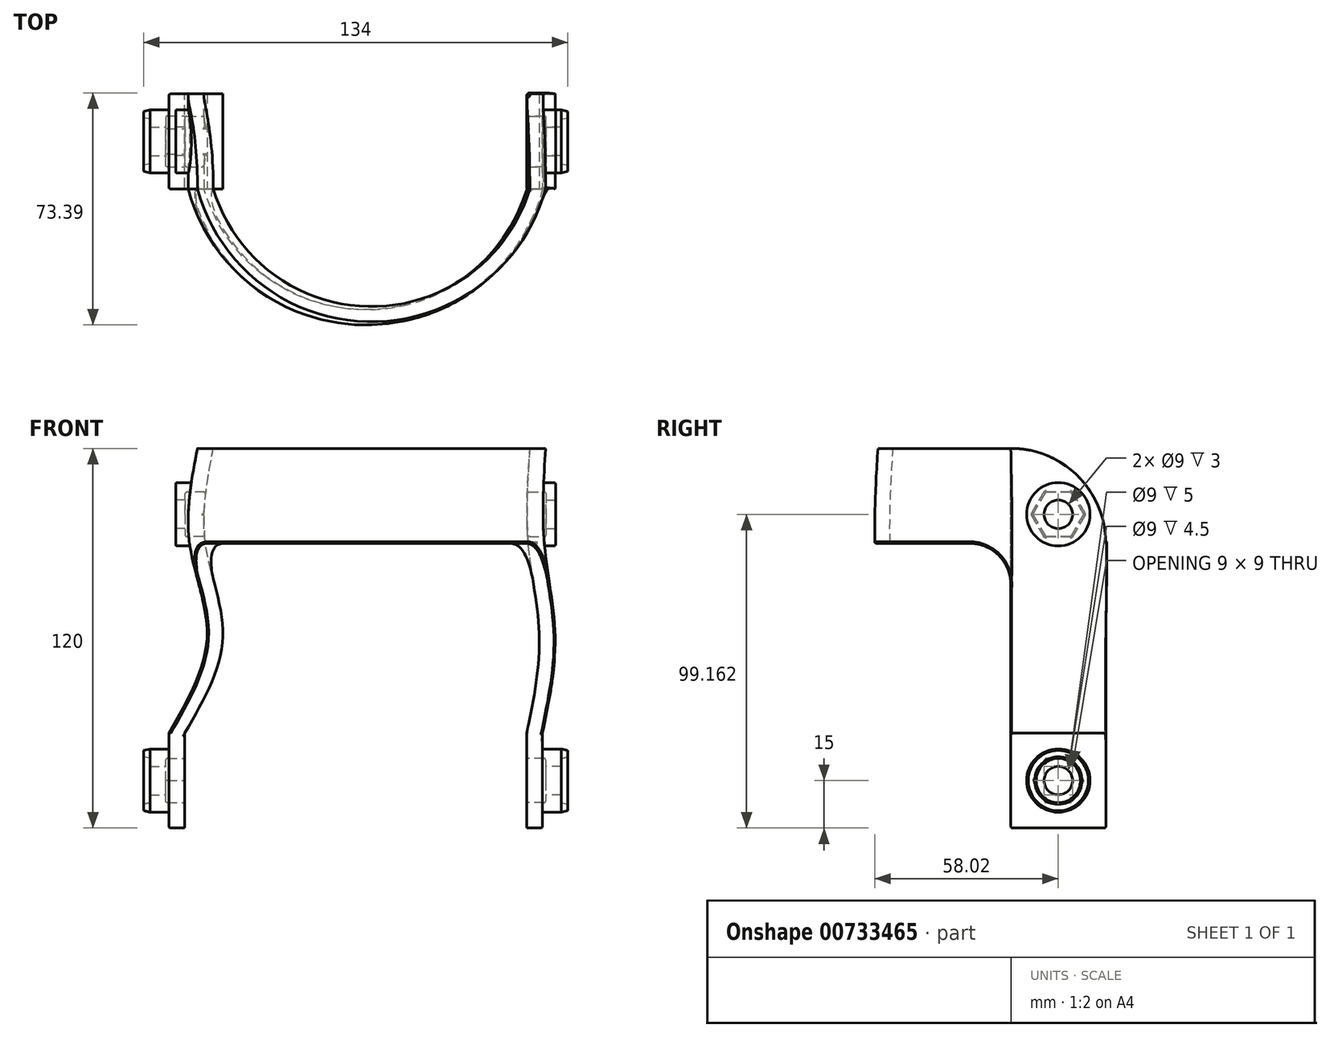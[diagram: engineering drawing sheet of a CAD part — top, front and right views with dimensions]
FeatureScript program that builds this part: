
annotation { "Feature Type Name" : "Feature", "Feature Type Description" : "" }
export const myFeature = defineFeature(function(context is Context, id is Id, definition is map)
    precondition{}
    {
        {
            var Q0;
            Q0=qCreatedBy(makeId("Top.planeOp"),FACE);
            cPlane(context, id + "F0", {"entities" : qUnion([Q0]), "cplaneType" : CPlaneType.OFFSET, "offset" : 30 * mm, "width" : 150 * mm, "height" : 150 * mm});
        }
        {
            var Q0;
            Q0=qCreatedBy(id+"F0.planeOp",FACE);
            var sketch = newSketch(context, id + "F1", { "sketchPlane" : qUnion([Q0])});
            skLineSegment(sketch, "E0", {"start": v(-54, 0) * mm, "end": v(-54, 15) * mm});
            skLineSegment(sketch, "E1", {"start": v(-54, 15) * mm, "end": v(-59, 15) * mm});
            skLineSegment(sketch, "E2", {"start": v(-59, 15) * mm, "end": v(-59, -15) * mm});
            skLineSegment(sketch, "E3", {"start": v(-54, -15) * mm, "end": v(-54, 0) * mm});
            skLineSegment(sketch, "E4", {"start": v(54, 0) * mm, "end": v(54, 15) * mm});
            skLineSegment(sketch, "E5", {"start": v(54, 15) * mm, "end": v(59, 15) * mm});
            skLineSegment(sketch, "E6", {"start": v(59, 15) * mm, "end": v(59, -15) * mm});
            skLineSegment(sketch, "E7", {"start": v(54, -15) * mm, "end": v(54, 0) * mm});
            skArc(sketch, "E8", {"start": v(-54, -15) * mm, "mid": v(0, -56.04) * mm, "end": v(54, -15) * mm});
            skArc(sketch, "E9", {"start": v(59, -15) * mm, "mid": v(0, -60.88) * mm, "end": v(-59, -15) * mm});
            skPoint(sketch, "E10", {"position": v(0, -56.04) * mm});
            skPoint(sketch, "E11", {"position": v(0, -60.88) * mm});
            skSolve(sketch);
        }
        {
            var Q0;
            Q0=qCreatedBy(makeId("Top.planeOp"),FACE);
            var sketch = newSketch(context, id + "F2", { "sketchPlane" : qUnion([Q0])});
            skLineSegment(sketch, "E12", {"start": v(-54, 0) * mm, "end": v(-54, 15) * mm});
            skLineSegment(sketch, "E13", {"start": v(-54, 15) * mm, "end": v(-59, 15) * mm});
            skLineSegment(sketch, "E14", {"start": v(-59, 15) * mm, "end": v(-59, -15) * mm});
            skLineSegment(sketch, "E15", {"start": v(-54, -15) * mm, "end": v(-54, 0) * mm});
            skLineSegment(sketch, "E16", {"start": v(54, 0) * mm, "end": v(54, 15) * mm});
            skLineSegment(sketch, "E17", {"start": v(54, 15) * mm, "end": v(59, 15) * mm});
            skLineSegment(sketch, "E18", {"start": v(59, 15) * mm, "end": v(59, -15) * mm});
            skLineSegment(sketch, "E19", {"start": v(54, -15) * mm, "end": v(54, 0) * mm});
            skArc(sketch, "E20", {"start": v(-54, -15) * mm, "mid": v(0, -56.04) * mm, "end": v(54, -15) * mm});
            skArc(sketch, "E21", {"start": v(59, -15) * mm, "mid": v(0, -60.88) * mm, "end": v(-59, -15) * mm});
            skPoint(sketch, "E22", {"position": v(0, -56.04) * mm});
            skPoint(sketch, "E23", {"position": v(0, -60.88) * mm});
            skSolve(sketch);
        }
        {
            var Q0;
            Q0=qCreatedBy(makeId("Top.planeOp"),FACE);
            cPlane(context, id + "F3", {"entities" : qUnion([Q0]), "cplaneType" : CPlaneType.OFFSET, "offset" : 60 * mm, "width" : 150 * mm, "height" : 150 * mm});
        }
        {
            var Q0;
            Q0=qCreatedBy(id+"F3.planeOp",FACE);
            var sketch = newSketch(context, id + "F4", { "sketchPlane" : qUnion([Q0])});
            skPoint(sketch, "E24", {"position": v(8, 0) * mm});
            skPoint(sketch, "E25", {"position": v(-42, 0) * mm});
            skPoint(sketch, "E26", {"position": v(58, 0) * mm});
            skLineSegment(sketch, "E27", {"start": v(-42, 0) * mm, "end": v(-42, -15) * mm});
            skLineSegment(sketch, "E28", {"start": v(-47, -15) * mm, "end": v(-47, 15) * mm});
            skLineSegment(sketch, "E29", {"start": v(-47, 15) * mm, "end": v(-42, 15) * mm});
            skLineSegment(sketch, "E30", {"start": v(-42, 15) * mm, "end": v(-42, 0) * mm});
            skLineSegment(sketch, "E31", {"start": v(58, 0) * mm, "end": v(58, 15) * mm});
            skLineSegment(sketch, "E32", {"start": v(58, 15) * mm, "end": v(63, 15) * mm});
            skLineSegment(sketch, "E33", {"start": v(63, 15) * mm, "end": v(63, -15) * mm});
            skLineSegment(sketch, "E34", {"start": v(58, -15) * mm, "end": v(58, 0) * mm});
            skArc(sketch, "E35", {"start": v(-42, -15) * mm, "mid": v(8, -52.2) * mm, "end": v(58, -15) * mm});
            skArc(sketch, "E36", {"start": v(-47, -15) * mm, "mid": v(8, -57) * mm, "end": v(63, -15) * mm});
            skSolve(sketch);
        }
        {
            var Q0;
            Q0=qCreatedBy(makeId("Top.planeOp"),FACE);
            cPlane(context, id + "F5", {"entities" : qUnion([Q0]), "cplaneType" : CPlaneType.OFFSET, "offset" : 90 * mm, "width" : 150 * mm, "height" : 150 * mm});
        }
        {
            var Q0;
            Q0=qCreatedBy(id+"F5.planeOp",FACE);
            var sketch = newSketch(context, id + "F6", { "sketchPlane" : qUnion([Q0])});
            skPoint(sketch, "E37", {"position": v(3.5, 0) * mm});
            skPoint(sketch, "E38", {"position": v(-47.5, 0) * mm});
            skPoint(sketch, "E39", {"position": v(54.5, 0) * mm});
            skLineSegment(sketch, "E40", {"start": v(-47.5, 0) * mm, "end": v(-47.5, 15) * mm});
            skLineSegment(sketch, "E41", {"start": v(-47.5, 15) * mm, "end": v(-52.5, 15) * mm});
            skLineSegment(sketch, "E42", {"start": v(-52.5, 15) * mm, "end": v(-52.5, -15) * mm});
            skLineSegment(sketch, "E43", {"start": v(-47.5, -15) * mm, "end": v(-47.5, 0) * mm});
            skLineSegment(sketch, "E44", {"start": v(54.5, 0) * mm, "end": v(54.5, 15.37) * mm});
            skLineSegment(sketch, "E45", {"start": v(54.5, 15.37) * mm, "end": v(59.6, 15.37) * mm});
            skLineSegment(sketch, "E46", {"start": v(59.6, 15.37) * mm, "end": v(59.6, -14.63) * mm});
            skLineSegment(sketch, "E47", {"start": v(54.5, -15) * mm, "end": v(54.5, 0) * mm});
            skArc(sketch, "E48", {"start": v(-47.5, -15) * mm, "mid": v(3.5, -53.16) * mm, "end": v(54.5, -15) * mm});
            skArc(sketch, "E49", {"start": v(-52.5, -15) * mm, "mid": v(3.69, -57.97) * mm, "end": v(59.6, -14.63) * mm});
            skSolve(sketch);
        }
        {
            var Q0;
            Q0=qCreatedBy(makeId("Top.planeOp"),FACE);
            cPlane(context, id + "F7", {"entities" : qUnion([Q0]), "cplaneType" : CPlaneType.OFFSET, "offset" : 120 * mm, "width" : 150 * mm, "height" : 150 * mm});
        }
        {
            var Q0;
            Q0=qCreatedBy(id+"F7.planeOp",FACE);
            var sketch = newSketch(context, id + "F8", { "sketchPlane" : qUnion([Q0])});
            skPoint(sketch, "E50", {"position": v(5, 0) * mm});
            skPoint(sketch, "E51", {"position": v(-45, 0) * mm});
            skPoint(sketch, "E52", {"position": v(55, 0) * mm});
            skLineSegment(sketch, "E53", {"start": v(-45, 0) * mm, "end": v(-45, 15) * mm});
            skLineSegment(sketch, "E54", {"start": v(-45, 15) * mm, "end": v(-50, 15) * mm});
            skLineSegment(sketch, "E55", {"start": v(-50, 15) * mm, "end": v(-50, -15) * mm});
            skLineSegment(sketch, "E56", {"start": v(-45, -15) * mm, "end": v(-45, 0) * mm});
            skLineSegment(sketch, "E57", {"start": v(55, 0) * mm, "end": v(55, -15) * mm});
            skLineSegment(sketch, "E58", {"start": v(60, -15) * mm, "end": v(60, 15) * mm});
            skLineSegment(sketch, "E59", {"start": v(60, 15) * mm, "end": v(55, 15) * mm});
            skLineSegment(sketch, "E60", {"start": v(55, 15) * mm, "end": v(55, 0) * mm});
            skArc(sketch, "E61", {"start": v(-45, -15) * mm, "mid": v(5, -52.2) * mm, "end": v(55, -15) * mm});
            skArc(sketch, "E62", {"start": v(-50, -15) * mm, "mid": v(5, -57) * mm, "end": v(60, -15) * mm});
            skSolve(sketch);
        }
        {
            var Q0;
            Q0=makeQuery(id+"F1.imprint","IMPRINT",FACE,{"disambiguationData":[TD([[makeQuery(id+"F1.imprint","IMPRINT",EDGE,{"derivedFrom":sQuery(id+"F1.wireOp",EDGE,"E0")}),1.0]])]});
            var Q1;
            Q1=makeQuery(id+"F4.imprint","IMPRINT",FACE,{"disambiguationData":[TD([[makeQuery(id+"F4.imprint","IMPRINT",EDGE,{"derivedFrom":sQuery(id+"F4.wireOp",EDGE,"E27")}),-1.0]])]});
            var Q2;
            Q2=makeQuery(id+"F6.imprint","IMPRINT",FACE,{"disambiguationData":[TD([[makeQuery(id+"F6.imprint","IMPRINT",EDGE,{"derivedFrom":sQuery(id+"F6.wireOp",EDGE,"E40")}),1.0]])]});
            var Q3;
            Q3=makeQuery(id+"F8.imprint","IMPRINT",FACE,{"disambiguationData":[TD([[makeQuery(id+"F8.imprint","IMPRINT",EDGE,{"derivedFrom":sQuery(id+"F8.wireOp",EDGE,"E53")}),1.0]])]});
            loft(context, id + "F9", {"sheetProfilesArray" : [{ "sheetProfileEntities" : qUnion([Q0]) }, { "sheetProfileEntities" : qUnion([Q1]) }, { "sheetProfileEntities" : qUnion([Q2]) }, { "sheetProfileEntities" : qUnion([Q3]) }]});
        }
        {
            var Q0;
            Q0=makeQuery(id+"F2.imprint","IMPRINT",FACE,{"disambiguationData":[TD([[makeQuery(id+"F2.imprint","IMPRINT",EDGE,{"derivedFrom":sQuery(id+"F2.wireOp",EDGE,"E12")}),1.0]])]});
            extrude(context, id + "F10", {"entities" : qUnion([Q0]), "operationType" : NewBodyOperationType.ADD, "depth" : 30 * mm, "offsetDistance" : 25 * mm});
        }
        {
            var Q0;
            Q0=qCreatedBy(makeId("Right.planeOp"),FACE);
            var sketch = newSketch(context, id + "F11", { "sketchPlane" : qUnion([Q0])});
            skPoint(sketch, "E63", {"position": v(82.65, 59.89) * mm});
            skPoint(sketch, "E64", {"position": v(-15, 120) * mm});
            skPoint(sketch, "E65", {"position": v(-15, 90) * mm});
            skArc(sketch, "E66", {"start": v(-15, 120) * mm, "mid": v(6.21, 111.21) * mm, "end": v(15, 90) * mm});
            skPoint(sketch, "E67", {"position": v(-28.01, 76.99) * mm});
            skArc(sketch, "E68", {"start": v(-15, 76.99) * mm, "mid": v(-18.81, 86.19) * mm, "end": v(-28.01, 90) * mm});
            skLineSegment(sketch, "E69", {"start": v(-15, 76.99) * mm, "end": v(-15, -61.51) * mm});
            skLineSegment(sketch, "E70", {"start": v(-15, -61.51) * mm, "end": v(-141.22, -61.51) * mm});
            skLineSegment(sketch, "E71", {"start": v(-141.22, -61.51) * mm, "end": v(-141.22, 174.74) * mm});
            skLineSegment(sketch, "E72", {"start": v(-141.22, 174.74) * mm, "end": v(85.32, 174.74) * mm});
            skLineSegment(sketch, "E73", {"start": v(85.32, 174.74) * mm, "end": v(15, 90) * mm});
            skLineSegment(sketch, "E74", {"start": v(-28.01, 90) * mm, "end": v(-81.35, 90) * mm});
            skLineSegment(sketch, "E75", {"start": v(-81.35, 90) * mm, "end": v(-81.35, 120) * mm});
            skLineSegment(sketch, "E76", {"start": v(-81.35, 120) * mm, "end": v(-15, 120) * mm});
            skSolve(sketch);
        }
        {
            var Q0;
            Q0=qSketchRegion(id+"F11",true);
            extrude(context, id + "F12", {"entities" : qUnion([Q0]), "operationType" : NewBodyOperationType.REMOVE, "oppositeDirection" : true, "depth" : 100 * mm, "offsetDistance" : 25 * mm, "hasSecondDirection" : true, "secondDirectionOppositeDirection" : false, "secondDirectionDepth" : 100 * mm});
        }
        {
            var Q0;
            Q0=makeQuery(id+"F10.opExtrude","SWEPT_FACE",FACE,{"disambiguationData":[OSD([sQuery(id+"F2.wireOp",EDGE,"E14")])]});
            var sketch = newSketch(context, id + "F13", { "sketchPlane" : qUnion([Q0])});
            skPoint(sketch, "E77", {"position": v(0, 15) * mm});
            skCircle(sketch, "E78", {"center": v(0, 15) * mm, "radius": 10 * mm});
            skSolve(sketch);
        }
        {
            var Q0;
            Q0=makeQuery(id+"F13.imprint","IMPRINT",FACE,{"disambiguationData":[TD([[makeQuery(id+"F13.imprint","IMPRINT",EDGE,{"derivedFrom":sQuery(id+"F13.wireOp",EDGE,"E78")}),1.0]])]});
            extrude(context, id + "F14", {"entities" : qUnion([Q0]), "operationType" : NewBodyOperationType.ADD, "depth" : 6 * mm, "offsetDistance" : 25 * mm});
        }
        {
            var Q0;
            Q0=qCreatedBy(makeId("Front.planeOp"),FACE);
            var sketch = newSketch(context, id + "F15", { "sketchPlane" : qUnion([Q0])});
            skPoint(sketch, "E79", {"position": v(-54, 15) * mm});
            skPoint(sketch, "E80", {"position": v(-49.01, 23.39) * mm});
            skPoint(sketch, "E81", {"position": v(-65, 15) * mm});
            skLineSegment(sketch, "E82", {"start": v(-65, 22) * mm, "end": v(-65, 25) * mm});
            skLineSegment(sketch, "E83", {"start": v(-65, 25) * mm, "end": v(-67, 24.5) * mm});
            skLineSegment(sketch, "E84", {"start": v(-67, 24.5) * mm, "end": v(-67, 22.5) * mm});
            skLineSegment(sketch, "E85", {"start": v(-67, 22.5) * mm, "end": v(-65, 22) * mm});
            skPoint(sketch, "E86", {"position": v(-65, 23.5) * mm});
            skPoint(sketch, "E87", {"position": v(-67, 23.5) * mm});
            skLineSegment(sketch, "E88", {"start": v(-65, 15) * mm, "end": v(-67, 15) * mm});
            skLineSegment(sketch, "E89", {"start": v(-65, 22) * mm, "end": v(-67, 22.5) * mm});
            skLineSegment(sketch, "E90", {"start": v(-67, 22.5) * mm, "end": v(-67, 24.5) * mm});
            skLineSegment(sketch, "E91", {"start": v(-67, 24.5) * mm, "end": v(-65, 25) * mm});
            skLineSegment(sketch, "E92", {"start": v(-65, 25) * mm, "end": v(-65, 22) * mm});
            skSolve(sketch);
        }
        {
            var Q0;
            Q0=qSketchRegion(id+"F15",true);
            var Q1;
            Q1=sQuery(id+"F15.wireOp",EDGE,"E88");
            revolve(context, id + "F16", {"operationType" : NewBodyOperationType.ADD, "surfaceOperationType" : NewSurfaceOperationType.NEW, "entities" : qUnion([Q0]), "axis" : qUnion([Q1]), "revolveType" : RevolveType.FULL});
        }
        {
            var Q0;
            Q0=makeQuery(id+"F10.opExtrude","SWEPT_FACE",FACE,{"disambiguationData":[OSD([sQuery(id+"F2.wireOp",EDGE,"E12"),sQuery(id+"F2.wireOp",EDGE,"E15")])]});
            var sketch = newSketch(context, id + "F17", { "sketchPlane" : qUnion([Q0])});
            skPoint(sketch, "E93", {"position": v(0, 15) * mm});
            skCircle(sketch, "E94", {"center": v(0, 15) * mm, "radius": 4.5 * mm});
            skSolve(sketch);
        }
        {
            var Q0;
            Q0=qSketchRegion(id+"F17",true);
            extrude(context, id + "F18", {"entities" : qUnion([Q0]), "operationType" : NewBodyOperationType.REMOVE, "oppositeDirection" : true, "depth" : 25 * mm, "offsetDistance" : 25 * mm});
        }
        {
            var Q0;
            Q0=makeQuery(id+"F10.opExtrude","SWEPT_FACE",FACE,{"disambiguationData":[OSD([sQuery(id+"F2.wireOp",EDGE,"E12"),sQuery(id+"F2.wireOp",EDGE,"E15")])]});
            var sketch = newSketch(context, id + "F19", { "sketchPlane" : qUnion([Q0])});
            skPoint(sketch, "E95", {"position": v(0, 15) * mm});
            skCircle(sketch, "E96", {"center": v(0, 15) * mm, "radius": 4.5 * mm});
            skSolve(sketch);
        }
        {
            var Q0;
            Q0=makeQuery(id+"F19.imprint","IMPRINT",FACE,{"disambiguationData":[TD([[makeQuery(id+"F19.imprint","IMPRINT",EDGE,{"derivedFrom":sQuery(id+"F19.wireOp",EDGE,"E96")}),-1.0]])]});
            var sketch = newSketch(context, id + "F20", { "sketchPlane" : qUnion([Q0])});
            skPoint(sketch, "E97", {"position": v(0, 15) * mm});
            skCircle(sketch, "E98", {"center": v(0, 15) * mm, "radius": 7 * mm});
            skPoint(sketch, "E99", {"position": v(0, 22) * mm});
            skCircle(sketch, "E100.cCircle", {"center": v(0, 15) * mm, "radius": 7 * mm, "construction": true});
            skLineSegment(sketch, "E100.0", {"start": v(-4.04, 22) * mm, "end": v(4.04, 22) * mm});
            skLineSegment(sketch, "E100.1", {"start": v(4.04, 22) * mm, "end": v(8.08, 15) * mm});
            skLineSegment(sketch, "E100.2", {"start": v(8.08, 15) * mm, "end": v(4.04, 8) * mm});
            skLineSegment(sketch, "E100.3", {"start": v(4.04, 8) * mm, "end": v(-4.04, 8) * mm});
            skLineSegment(sketch, "E100.4", {"start": v(-4.04, 8) * mm, "end": v(-8.08, 15) * mm});
            skLineSegment(sketch, "E100.5", {"start": v(-8.08, 15) * mm, "end": v(-4.04, 22) * mm});
            skSolve(sketch);
        }
        {
            var Q0;
            Q0=qSketchRegion(id+"F20",true);
            extrude(context, id + "F21", {"entities" : qUnion([Q0]), "operationType" : NewBodyOperationType.REMOVE, "oppositeDirection" : true, "depth" : 6 * mm, "offsetDistance" : 25 * mm});
        }
        {
            var Q0;
            Q0=makeQuery(id+"F10.opExtrude","SWEPT_FACE",FACE,{"disambiguationData":[OSD([sQuery(id+"F2.wireOp",EDGE,"E18")])]});
            var sketch = newSketch(context, id + "F22", { "sketchPlane" : qUnion([Q0])});
            skPoint(sketch, "E101", {"position": v(0, 15) * mm});
            skCircle(sketch, "E102", {"center": v(0, 15) * mm, "radius": 10 * mm});
            skSolve(sketch);
        }
        {
            var Q0;
            Q0=qSketchRegion(id+"F22",true);
            extrude(context, id + "F23", {"entities" : qUnion([Q0]), "operationType" : NewBodyOperationType.ADD, "depth" : 6 * mm, "offsetDistance" : 25 * mm});
        }
        {
            var Q0;
            Q0=qCreatedBy(makeId("Front.planeOp"),FACE);
            var sketch = newSketch(context, id + "F24", { "sketchPlane" : qUnion([Q0])});
            skPoint(sketch, "E103", {"position": v(54, 15) * mm});
            skPoint(sketch, "E104", {"position": v(32.82, 5.22) * mm});
            skPoint(sketch, "E105", {"position": v(65, 15) * mm});
            skLineSegment(sketch, "E106", {"start": v(65, 8) * mm, "end": v(65, 5) * mm});
            skLineSegment(sketch, "E107", {"start": v(65, 5) * mm, "end": v(67, 5.5) * mm});
            skLineSegment(sketch, "E108", {"start": v(67, 5.5) * mm, "end": v(67, 7.5) * mm});
            skLineSegment(sketch, "E109", {"start": v(67, 7.5) * mm, "end": v(65, 8) * mm});
            skPoint(sketch, "E110", {"position": v(65, 6.5) * mm});
            skPoint(sketch, "E111", {"position": v(67, 6.5) * mm});
            skLineSegment(sketch, "E112", {"start": v(65, 15) * mm, "end": v(67, 15) * mm});
            skLineSegment(sketch, "E113", {"start": v(65, 8) * mm, "end": v(67, 7.5) * mm});
            skLineSegment(sketch, "E114", {"start": v(67, 7.5) * mm, "end": v(67, 5.5) * mm});
            skLineSegment(sketch, "E115", {"start": v(67, 5.5) * mm, "end": v(65, 5) * mm});
            skLineSegment(sketch, "E116", {"start": v(65, 5) * mm, "end": v(65, 8) * mm});
            skSolve(sketch);
        }
        {
            var Q0;
            Q0=qSketchRegion(id+"F24",true);
            var Q1;
            Q1=sQuery(id+"F24.wireOp",EDGE,"E112");
            revolve(context, id + "F25", {"operationType" : NewBodyOperationType.ADD, "surfaceOperationType" : NewSurfaceOperationType.NEW, "entities" : qUnion([Q0]), "axis" : qUnion([Q1]), "revolveType" : RevolveType.FULL});
        }
        {
            var Q0;
            Q0=makeQuery(id+"F10.opExtrude","SWEPT_FACE",FACE,{"disambiguationData":[OSD([sQuery(id+"F2.wireOp",EDGE,"E16"),sQuery(id+"F2.wireOp",EDGE,"E19")])]});
            var sketch = newSketch(context, id + "F26", { "sketchPlane" : qUnion([Q0])});
            skPoint(sketch, "E117", {"position": v(0, 15) * mm});
            skCircle(sketch, "E118", {"center": v(0, 15) * mm, "radius": 4.5 * mm});
            skSolve(sketch);
        }
        {
            var Q0;
            Q0=qSketchRegion(id+"F26",true);
            extrude(context, id + "F27", {"entities" : qUnion([Q0]), "operationType" : NewBodyOperationType.REMOVE, "oppositeDirection" : true, "depth" : 25 * mm, "offsetDistance" : 25 * mm});
        }
        {
            var Q0;
            Q0=makeQuery(id+"F10.opExtrude","SWEPT_FACE",FACE,{"disambiguationData":[OSD([sQuery(id+"F2.wireOp",EDGE,"E16"),sQuery(id+"F2.wireOp",EDGE,"E19")])]});
            var sketch = newSketch(context, id + "F28", { "sketchPlane" : qUnion([Q0])});
            skPoint(sketch, "E119", {"position": v(0, 15) * mm});
            skCircle(sketch, "E120", {"center": v(0, 15) * mm, "radius": 7 * mm});
            skPoint(sketch, "E121", {"position": v(0, 22) * mm});
            skCircle(sketch, "E122.cCircle", {"center": v(0, 15) * mm, "radius": 7 * mm, "construction": true});
            skLineSegment(sketch, "E122.0", {"start": v(-4.04, 22) * mm, "end": v(4.04, 22) * mm});
            skLineSegment(sketch, "E122.1", {"start": v(4.04, 22) * mm, "end": v(8.08, 15) * mm});
            skLineSegment(sketch, "E122.2", {"start": v(8.08, 15) * mm, "end": v(4.04, 8) * mm});
            skLineSegment(sketch, "E122.3", {"start": v(4.04, 8) * mm, "end": v(-4.04, 8) * mm});
            skLineSegment(sketch, "E122.4", {"start": v(-4.04, 8) * mm, "end": v(-8.08, 15) * mm});
            skLineSegment(sketch, "E122.5", {"start": v(-8.08, 15) * mm, "end": v(-4.04, 22) * mm});
            skSolve(sketch);
        }
        {
            var Q0;
            Q0=qSketchRegion(id+"F28",true);
            extrude(context, id + "F29", {"entities" : qUnion([Q0]), "operationType" : NewBodyOperationType.REMOVE, "oppositeDirection" : true, "depth" : 6 * mm, "offsetDistance" : 25 * mm});
        }
        {
            var Q0;
            Q0=qCreatedBy(makeId("Right.planeOp"),FACE);
            cPlane(context, id + "F30", {"entities" : qUnion([Q0]), "cplaneType" : CPlaneType.OFFSET, "offset" : 57.3 * mm, "oppositeDirection" : true, "width" : 150 * mm, "height" : 150 * mm});
        }
        {
            var Q0;
            Q0=qCreatedBy(makeId("Front.planeOp"),FACE);
            var sketch = newSketch(context, id + "F31", { "sketchPlane" : qUnion([Q0])});
            skPoint(sketch, "E123", {"position": v(-47.9, 99.16) * mm});
            skPoint(sketch, "E124", {"position": v(-56.9, 99.16) * mm});
            skPoint(sketch, "E125", {"position": v(-57.3, 99.16) * mm});
            skSolve(sketch);
        }
        {
            var Q0;
            Q0=qCreatedBy(id+"F30.planeOp",FACE);
            cPlane(context, id + "F32", {"entities" : qUnion([Q0]), "cplaneType" : CPlaneType.OFFSET, "offset" : 0.4 * mm, "width" : 150 * mm, "height" : 150 * mm});
        }
        {
            var Q0;
            Q0=qCreatedBy(id+"F32.planeOp",FACE);
            var sketch = newSketch(context, id + "F33", { "sketchPlane" : qUnion([Q0])});
            skPoint(sketch, "E126", {"position": v(0, 99.16) * mm});
            skCircle(sketch, "E127", {"center": v(0, 99.16) * mm, "radius": 10 * mm});
            skSolve(sketch);
        }
        {
            var Q0;
            Q0=qSketchRegion(id+"F33",true);
            extrude(context, id + "F34", {"entities" : qUnion([Q0]), "operationType" : NewBodyOperationType.ADD, "depth" : 5 * mm, "offsetDistance" : 25 * mm});
        }
        {
            var Q0;
            Q0=makeQuery(id+"F34.opExtrude","CAP_FACE",FACE,{"disambiguationData":[OSD([sQuery(id+"F33.wireOp",EDGE,"E127")])],"isStart":true});
            var sketch = newSketch(context, id + "F35", { "sketchPlane" : qUnion([Q0])});
            skCircle(sketch, "E128", {"center": v(0, 99.16) * mm, "radius": 4.5 * mm});
            skSolve(sketch);
        }
        {
            var Q0;
            Q0=qSketchRegion(id+"F35",true);
            extrude(context, id + "F36", {"entities" : qUnion([Q0]), "operationType" : NewBodyOperationType.REMOVE, "oppositeDirection" : true, "depth" : 25 * mm, "offsetDistance" : 25 * mm});
        }
        {
            var Q0;
            Q0=makeQuery(id+"F34.opExtrude","CAP_FACE",FACE,{"disambiguationData":[OSD([sQuery(id+"F33.wireOp",EDGE,"E127")])],"isStart":true});
            var sketch = newSketch(context, id + "F37", { "sketchPlane" : qUnion([Q0])});
            skPoint(sketch, "E129", {"position": v(-6.55, 97.38) * mm});
            skPoint(sketch, "E130", {"position": v(0, 99.16) * mm});
            skCircle(sketch, "E131", {"center": v(0, 99.16) * mm, "radius": 7 * mm});
            skPoint(sketch, "E132", {"position": v(0, 106.16) * mm});
            skCircle(sketch, "E133.cCircle", {"center": v(0, 99.16) * mm, "radius": 7 * mm, "construction": true});
            skLineSegment(sketch, "E133.0", {"start": v(-4.04, 106.16) * mm, "end": v(4.04, 106.16) * mm});
            skLineSegment(sketch, "E133.1", {"start": v(4.04, 106.16) * mm, "end": v(8.08, 99.16) * mm});
            skLineSegment(sketch, "E133.2", {"start": v(8.08, 99.16) * mm, "end": v(4.04, 92.16) * mm});
            skLineSegment(sketch, "E133.3", {"start": v(4.04, 92.16) * mm, "end": v(-4.04, 92.16) * mm});
            skLineSegment(sketch, "E133.4", {"start": v(-4.04, 92.16) * mm, "end": v(-8.08, 99.16) * mm});
            skLineSegment(sketch, "E133.5", {"start": v(-8.08, 99.16) * mm, "end": v(-4.04, 106.16) * mm});
            skSolve(sketch);
        }
        {
            var Q0;
            Q0=qSketchRegion(id+"F37",true);
            extrude(context, id + "F38", {"entities" : qUnion([Q0]), "operationType" : NewBodyOperationType.REMOVE, "oppositeDirection" : true, "depth" : 25 * mm, "offsetDistance" : 25 * mm, "hasSecondDirection" : true, "secondDirectionOppositeDirection" : true, "secondDirectionDepth" : 3 * mm});
        }
        {
            var Q0;
            Q0=qCreatedBy(makeId("Right.planeOp"),FACE);
            cPlane(context, id + "F39", {"entities" : qUnion([Q0]), "cplaneType" : CPlaneType.OFFSET, "offset" : 67 * mm, "width" : 150 * mm, "height" : 150 * mm});
        }
        {
            var Q0;
            Q0=qCreatedBy(id+"F39.planeOp",FACE);
            cPlane(context, id + "F40", {"entities" : qUnion([Q0]), "cplaneType" : CPlaneType.OFFSET, "offset" : 3.84 * mm, "oppositeDirection" : true, "width" : 150 * mm, "height" : 150 * mm});
        }
        {
            var Q0;
            Q0=qCreatedBy(id+"F40.planeOp",FACE);
            var sketch = newSketch(context, id + "F41", { "sketchPlane" : qUnion([Q0])});
            skPoint(sketch, "E134", {"position": v(0, 99.16) * mm});
            skCircle(sketch, "E135", {"center": v(0, 99.16) * mm, "radius": 10 * mm});
            skSolve(sketch);
        }
        {
            var Q0;
            Q0=qSketchRegion(id+"F41",true);
            extrude(context, id + "F42", {"entities" : qUnion([Q0]), "operationType" : NewBodyOperationType.ADD, "oppositeDirection" : true, "depth" : 5 * mm, "offsetDistance" : 25 * mm});
        }
        {
            var Q0;
            Q0=makeQuery(id+"F42.opExtrude","CAP_FACE",FACE,{"disambiguationData":[OSD([sQuery(id+"F41.wireOp",EDGE,"E135")])],"isStart":true});
            var sketch = newSketch(context, id + "F43", { "sketchPlane" : qUnion([Q0])});
            skPoint(sketch, "E136", {"position": v(0, 99.16) * mm});
            skCircle(sketch, "E137", {"center": v(0, 99.16) * mm, "radius": 4.5 * mm});
            skSolve(sketch);
        }
        {
            var Q0;
            Q0=qSketchRegion(id+"F43",true);
            extrude(context, id + "F44", {"entities" : qUnion([Q0]), "operationType" : NewBodyOperationType.REMOVE, "oppositeDirection" : true, "depth" : 25 * mm, "offsetDistance" : 25 * mm});
        }
        {
            var Q0;
            Q0=makeQuery(id+"F42.opExtrude","CAP_FACE",FACE,{"disambiguationData":[OSD([sQuery(id+"F41.wireOp",EDGE,"E135")])],"isStart":true});
            var sketch = newSketch(context, id + "F45", { "sketchPlane" : qUnion([Q0])});
            skPoint(sketch, "E138", {"position": v(-0.57, 99.82) * mm});
            skPoint(sketch, "E139", {"position": v(0, 99.16) * mm});
            skCircle(sketch, "E140", {"center": v(0, 99.16) * mm, "radius": 7 * mm});
            skPoint(sketch, "E141", {"position": v(0, 106.16) * mm});
            skCircle(sketch, "E142.cCircle", {"center": v(0, 99.16) * mm, "radius": 7 * mm, "construction": true});
            skLineSegment(sketch, "E142.0", {"start": v(-4.04, 106.16) * mm, "end": v(4.04, 106.16) * mm});
            skLineSegment(sketch, "E142.1", {"start": v(4.04, 106.16) * mm, "end": v(8.08, 99.16) * mm});
            skLineSegment(sketch, "E142.2", {"start": v(8.08, 99.16) * mm, "end": v(4.04, 92.16) * mm});
            skLineSegment(sketch, "E142.3", {"start": v(4.04, 92.16) * mm, "end": v(-4.04, 92.16) * mm});
            skLineSegment(sketch, "E142.4", {"start": v(-4.04, 92.16) * mm, "end": v(-8.08, 99.16) * mm});
            skLineSegment(sketch, "E142.5", {"start": v(-8.08, 99.16) * mm, "end": v(-4.04, 106.16) * mm});
            skSolve(sketch);
        }
        {
            var Q0;
            Q0=qSketchRegion(id+"F45",true);
            extrude(context, id + "F46", {"entities" : qUnion([Q0]), "operationType" : NewBodyOperationType.REMOVE, "oppositeDirection" : true, "depth" : 25 * mm, "offsetDistance" : 25 * mm, "hasSecondDirection" : true, "secondDirectionOppositeDirection" : true, "secondDirectionDepth" : 3 * mm});
        }
        {
            var Q0;
            Q0=makeQuery(id+"F12.boolean.opBoolean","INTERSECT",EDGE,{"derivedFrom":[makeQuery(id+"F9.opLoft","SWEPT_FACE",FACE,{"disambiguationData":[OSD([sQuery(id+"F1.wireOp",EDGE,"E2"),sQuery(id+"F1.wireOp",EDGE,"E6"),sQuery(id+"F1.wireOp",EDGE,"E9"),sQuery(id+"F4.wireOp",EDGE,"E28"),sQuery(id+"F4.wireOp",EDGE,"E33"),sQuery(id+"F4.wireOp",EDGE,"E36")])]}),makeQuery(id+"F12.opExtrude","SWEPT_FACE",FACE,{"disambiguationData":[OSD([sQuery(id+"F11.wireOp",EDGE,"E74")])]})]});
            var Q1;
            Q1=makeQuery(id+"F10.opExtrude","CAP_EDGE",EDGE,{"disambiguationData":[OSD([sQuery(id+"F2.wireOp",EDGE,"E14")])],"isStart":true});
            var Q2;
            Q2=makeQuery(id+"F10.opExtrude","SWEPT_EDGE",EDGE,{"disambiguationData":[OSD([sQuery(id+"F2.wireOp",EDGE,"E14"),sQuery(id+"F2.wireOp",EDGE,"E21")])]});
            var Q3;
            Q3=makeQuery(id+"F10.opExtrude","SWEPT_EDGE",EDGE,{"disambiguationData":[OSD([sQuery(id+"F2.wireOp",EDGE,"E13"),sQuery(id+"F2.wireOp",EDGE,"E14")])]});
            var Q4;
            Q4=makeQuery(id+"F10.opExtrude","CAP_EDGE",EDGE,{"disambiguationData":[OSD([sQuery(id+"F2.wireOp",EDGE,"E13")])],"isStart":true});
            var Q5;
            Q5=makeQuery(id+"F12.boolean.opBoolean","INTERSECT",EDGE,{"disambiguationData":[OD(0.0)],"derivedFrom":[makeQuery(id+"F10.opExtrude","CAP_FACE",FACE,{"disambiguationData":[OSD([sQuery(id+"F2.wireOp",EDGE,"E12"),sQuery(id+"F2.wireOp",EDGE,"E13"),sQuery(id+"F2.wireOp",EDGE,"E14"),sQuery(id+"F2.wireOp",EDGE,"E15"),sQuery(id+"F2.wireOp",EDGE,"E16"),sQuery(id+"F2.wireOp",EDGE,"E17"),sQuery(id+"F2.wireOp",EDGE,"E18"),sQuery(id+"F2.wireOp",EDGE,"E19"),sQuery(id+"F2.wireOp",EDGE,"E20"),sQuery(id+"F2.wireOp",EDGE,"E21")])],"isStart":true}),makeQuery(id+"F12.opExtrude","SWEPT_FACE",FACE,{"disambiguationData":[OSD([sQuery(id+"F11.wireOp",EDGE,"E69")])]})]});
            var Q6;
            Q6=makeQuery(id+"F10.opExtrude","CAP_EDGE",EDGE,{"disambiguationData":[OSD([sQuery(id+"F2.wireOp",EDGE,"E12"),sQuery(id+"F2.wireOp",EDGE,"E15")])],"isStart":true});
            var Q7;
            Q7=makeQuery(id+"F10.opExtrude","SWEPT_EDGE",EDGE,{"disambiguationData":[OSD([sQuery(id+"F2.wireOp",EDGE,"E12"),sQuery(id+"F2.wireOp",EDGE,"E13")])]});
            var Q8;
            Q8=makeQuery(id+"F10.opExtrude","SWEPT_EDGE",EDGE,{"disambiguationData":[OSD([sQuery(id+"F2.wireOp",EDGE,"E15"),sQuery(id+"F2.wireOp",EDGE,"E20")])]});
            var Q9;
            Q9=makeQuery(id+"F21.boolean.opBoolean","COPY",EDGE,{"derivedFrom":makeQuery(id+"F21.opExtrude","CAP_EDGE",EDGE,{"disambiguationData":[OSD([sQuery(id+"F20.wireOp",EDGE,"E100.1")])],"isStart":true})});
            var Q10;
            Q10=makeQuery(id+"F21.boolean.opBoolean","COPY",EDGE,{"derivedFrom":makeQuery(id+"F21.opExtrude","CAP_EDGE",EDGE,{"disambiguationData":[OSD([sQuery(id+"F20.wireOp",EDGE,"E100.0")])],"isStart":true})});
            var Q11;
            Q11=makeQuery(id+"F21.boolean.opBoolean","COPY",EDGE,{"derivedFrom":makeQuery(id+"F21.opExtrude","CAP_EDGE",EDGE,{"disambiguationData":[OSD([sQuery(id+"F20.wireOp",EDGE,"E100.5")])],"isStart":true})});
            var Q12;
            Q12=makeQuery(id+"F21.boolean.opBoolean","COPY",EDGE,{"derivedFrom":makeQuery(id+"F21.opExtrude","CAP_EDGE",EDGE,{"disambiguationData":[OSD([sQuery(id+"F20.wireOp",EDGE,"E100.4")])],"isStart":true})});
            var Q13;
            Q13=makeQuery(id+"F21.boolean.opBoolean","COPY",EDGE,{"derivedFrom":makeQuery(id+"F21.opExtrude","CAP_EDGE",EDGE,{"disambiguationData":[OSD([sQuery(id+"F20.wireOp",EDGE,"E100.3")])],"isStart":true})});
            var Q14;
            Q14=makeQuery(id+"F21.boolean.opBoolean","COPY",EDGE,{"derivedFrom":makeQuery(id+"F21.opExtrude","CAP_EDGE",EDGE,{"disambiguationData":[OSD([sQuery(id+"F20.wireOp",EDGE,"E100.2")])],"isStart":true})});
            var Q15;
            Q15=makeQuery(id+"F21.boolean.opBoolean","COPY",FACE,{"derivedFrom":makeQuery(id+"F21.opExtrude","CAP_FACE",FACE,{"disambiguationData":[OSD([sQuery(id+"F20.wireOp",EDGE,"E100.0"),sQuery(id+"F20.wireOp",EDGE,"E100.1"),sQuery(id+"F20.wireOp",EDGE,"E100.2"),sQuery(id+"F20.wireOp",EDGE,"E100.3"),sQuery(id+"F20.wireOp",EDGE,"E100.4"),sQuery(id+"F20.wireOp",EDGE,"E100.5")])],"isStart":false})});
            fillet(context, id + "F47", {"entities" : qUnion([Q0, Q1, Q2, Q3, Q4, Q5, Q6, Q7, Q8, Q9, Q10, Q11, Q12, Q13, Q14, Q15]), "radius" : 0.5 * mm, "tangentPropagation" : true, "allowEdgeOverflow" : false});
        }
        {
            var Q0;
            Q0=makeQuery(id+"F29.boolean.opBoolean","COPY",FACE,{"derivedFrom":makeQuery(id+"F29.opExtrude","SWEPT_FACE",FACE,{"disambiguationData":[OSD([sQuery(id+"F28.wireOp",EDGE,"E122.4")])]})});
            var Q1;
            Q1=makeQuery(id+"F29.boolean.opBoolean","COPY",FACE,{"derivedFrom":makeQuery(id+"F29.opExtrude","SWEPT_FACE",FACE,{"disambiguationData":[OSD([sQuery(id+"F28.wireOp",EDGE,"E122.5")])]})});
            var Q2;
            Q2=makeQuery(id+"F29.boolean.opBoolean","COPY",FACE,{"derivedFrom":makeQuery(id+"F29.opExtrude","SWEPT_FACE",FACE,{"disambiguationData":[OSD([sQuery(id+"F28.wireOp",EDGE,"E122.0")])]})});
            var Q3;
            Q3=makeQuery(id+"F29.boolean.opBoolean","COPY",FACE,{"derivedFrom":makeQuery(id+"F29.opExtrude","SWEPT_FACE",FACE,{"disambiguationData":[OSD([sQuery(id+"F28.wireOp",EDGE,"E122.1")])]})});
            var Q4;
            Q4=makeQuery(id+"F29.boolean.opBoolean","COPY",FACE,{"derivedFrom":makeQuery(id+"F29.opExtrude","SWEPT_FACE",FACE,{"disambiguationData":[OSD([sQuery(id+"F28.wireOp",EDGE,"E122.3")])]})});
            var Q5;
            Q5=makeQuery(id+"F29.boolean.opBoolean","COPY",FACE,{"derivedFrom":makeQuery(id+"F29.opExtrude","SWEPT_FACE",FACE,{"disambiguationData":[OSD([sQuery(id+"F28.wireOp",EDGE,"E122.2")])]})});
            var Q6;
            Q6=makeQuery(id+"F10.opExtrude","SWEPT_EDGE",EDGE,{"disambiguationData":[OSD([sQuery(id+"F2.wireOp",EDGE,"E18"),sQuery(id+"F2.wireOp",EDGE,"E21")])]});
            var Q7;
            Q7=makeQuery(id+"F10.opExtrude","SWEPT_EDGE",EDGE,{"disambiguationData":[OSD([sQuery(id+"F2.wireOp",EDGE,"E19"),sQuery(id+"F2.wireOp",EDGE,"E20")])]});
            var Q8;
            Q8=makeQuery(id+"F12.boolean.opBoolean","INTERSECT",EDGE,{"disambiguationData":[OD(1.0)],"derivedFrom":[makeQuery(id+"F10.opExtrude","CAP_FACE",FACE,{"disambiguationData":[OSD([sQuery(id+"F2.wireOp",EDGE,"E12"),sQuery(id+"F2.wireOp",EDGE,"E13"),sQuery(id+"F2.wireOp",EDGE,"E14"),sQuery(id+"F2.wireOp",EDGE,"E15"),sQuery(id+"F2.wireOp",EDGE,"E16"),sQuery(id+"F2.wireOp",EDGE,"E17"),sQuery(id+"F2.wireOp",EDGE,"E18"),sQuery(id+"F2.wireOp",EDGE,"E19"),sQuery(id+"F2.wireOp",EDGE,"E20"),sQuery(id+"F2.wireOp",EDGE,"E21")])],"isStart":true}),makeQuery(id+"F12.opExtrude","SWEPT_FACE",FACE,{"disambiguationData":[OSD([sQuery(id+"F11.wireOp",EDGE,"E69")])]})]});
            var Q9;
            Q9=makeQuery(id+"F10.opExtrude","CAP_EDGE",EDGE,{"disambiguationData":[OSD([sQuery(id+"F2.wireOp",EDGE,"E16"),sQuery(id+"F2.wireOp",EDGE,"E19")])],"isStart":true});
            var Q10;
            Q10=makeQuery(id+"F10.opExtrude","CAP_EDGE",EDGE,{"disambiguationData":[OSD([sQuery(id+"F2.wireOp",EDGE,"E18")])],"isStart":true});
            var Q11;
            Q11=makeQuery(id+"F10.opExtrude","SWEPT_EDGE",EDGE,{"disambiguationData":[OSD([sQuery(id+"F2.wireOp",EDGE,"E17"),sQuery(id+"F2.wireOp",EDGE,"E18")])]});
            var Q12;
            Q12=makeQuery(id+"F10.opExtrude","SWEPT_EDGE",EDGE,{"disambiguationData":[OSD([sQuery(id+"F2.wireOp",EDGE,"E16"),sQuery(id+"F2.wireOp",EDGE,"E17")])]});
            var Q13;
            Q13=makeQuery(id+"F10.opExtrude","CAP_EDGE",EDGE,{"disambiguationData":[OSD([sQuery(id+"F2.wireOp",EDGE,"E17")])],"isStart":true});
            fillet(context, id + "F48", {"entities" : qUnion([Q0, Q1, Q2, Q3, Q4, Q5, Q6, Q7, Q8, Q9, Q10, Q11, Q12, Q13]), "radius" : 0.5 * mm, "tangentPropagation" : true, "allowEdgeOverflow" : false});
        }
        {
            var Q0;
            Q0=makeQuery(id+"F38.boolean.opBoolean","COPY",FACE,{"derivedFrom":makeQuery(id+"F38.opExtrude","SWEPT_FACE",FACE,{"disambiguationData":[OSD([sQuery(id+"F37.wireOp",EDGE,"E133.0")])]})});
            var Q1;
            Q1=makeQuery(id+"F38.boolean.opBoolean","COPY",FACE,{"derivedFrom":makeQuery(id+"F38.opExtrude","SWEPT_FACE",FACE,{"disambiguationData":[OSD([sQuery(id+"F37.wireOp",EDGE,"E133.5")])]})});
            var Q2;
            Q2=makeQuery(id+"F38.boolean.opBoolean","COPY",FACE,{"derivedFrom":makeQuery(id+"F38.opExtrude","SWEPT_FACE",FACE,{"disambiguationData":[OSD([sQuery(id+"F37.wireOp",EDGE,"E133.4")])]})});
            var Q3;
            Q3=makeQuery(id+"F38.boolean.opBoolean","COPY",FACE,{"derivedFrom":makeQuery(id+"F38.opExtrude","SWEPT_FACE",FACE,{"disambiguationData":[OSD([sQuery(id+"F37.wireOp",EDGE,"E133.1")])]})});
            var Q4;
            Q4=makeQuery(id+"F38.boolean.opBoolean","COPY",FACE,{"derivedFrom":makeQuery(id+"F38.opExtrude","SWEPT_FACE",FACE,{"disambiguationData":[OSD([sQuery(id+"F37.wireOp",EDGE,"E133.2")])]})});
            var Q5;
            Q5=makeQuery(id+"F38.boolean.opBoolean","COPY",FACE,{"derivedFrom":makeQuery(id+"F38.opExtrude","SWEPT_FACE",FACE,{"disambiguationData":[OSD([sQuery(id+"F37.wireOp",EDGE,"E133.3")])]})});
            fillet(context, id + "F49", {"entities" : qUnion([Q0, Q1, Q2, Q3, Q4, Q5]), "radius" : 0.5 * mm, "tangentPropagation" : true, "allowEdgeOverflow" : false});
        }
        {
            var Q0;
            Q0=makeQuery(id+"F46.boolean.opBoolean","COPY",FACE,{"derivedFrom":makeQuery(id+"F46.opExtrude","SWEPT_FACE",FACE,{"disambiguationData":[OSD([sQuery(id+"F45.wireOp",EDGE,"E142.5")])]})});
            var Q1;
            Q1=makeQuery(id+"F46.boolean.opBoolean","COPY",FACE,{"derivedFrom":makeQuery(id+"F46.opExtrude","SWEPT_FACE",FACE,{"disambiguationData":[OSD([sQuery(id+"F45.wireOp",EDGE,"E142.0")])]})});
            var Q2;
            Q2=makeQuery(id+"F46.boolean.opBoolean","COPY",FACE,{"derivedFrom":makeQuery(id+"F46.opExtrude","SWEPT_FACE",FACE,{"disambiguationData":[OSD([sQuery(id+"F45.wireOp",EDGE,"E142.4")])]})});
            var Q3;
            Q3=makeQuery(id+"F46.boolean.opBoolean","COPY",FACE,{"derivedFrom":makeQuery(id+"F46.opExtrude","SWEPT_FACE",FACE,{"disambiguationData":[OSD([sQuery(id+"F45.wireOp",EDGE,"E142.3")])]})});
            var Q4;
            Q4=makeQuery(id+"F46.boolean.opBoolean","COPY",FACE,{"derivedFrom":makeQuery(id+"F46.opExtrude","SWEPT_FACE",FACE,{"disambiguationData":[OSD([sQuery(id+"F45.wireOp",EDGE,"E142.2")])]})});
            var Q5;
            Q5=makeQuery(id+"F46.boolean.opBoolean","COPY",FACE,{"derivedFrom":makeQuery(id+"F46.opExtrude","SWEPT_FACE",FACE,{"disambiguationData":[OSD([sQuery(id+"F45.wireOp",EDGE,"E142.1")])]})});
            fillet(context, id + "F50", {"entities" : qUnion([Q0, Q1, Q2, Q3, Q4, Q5]), "radius" : 0.5 * mm, "tangentPropagation" : true, "allowEdgeOverflow" : false});
        }
        {
            var Q0;
            Q0=makeQuery(id+"F42.opExtrude","CAP_EDGE",EDGE,{"disambiguationData":[OSD([sQuery(id+"F41.wireOp",EDGE,"E135")])],"isStart":true});
            var Q1;
            Q1=makeQuery(id+"F34.opExtrude","CAP_EDGE",EDGE,{"disambiguationData":[OSD([sQuery(id+"F33.wireOp",EDGE,"E127")])],"isStart":true});
            fillet(context, id + "F51", {"entities" : qUnion([Q0, Q1]), "radius" : 0.5 * mm, "tangentPropagation" : true, "allowEdgeOverflow" : false});
        }
    });
